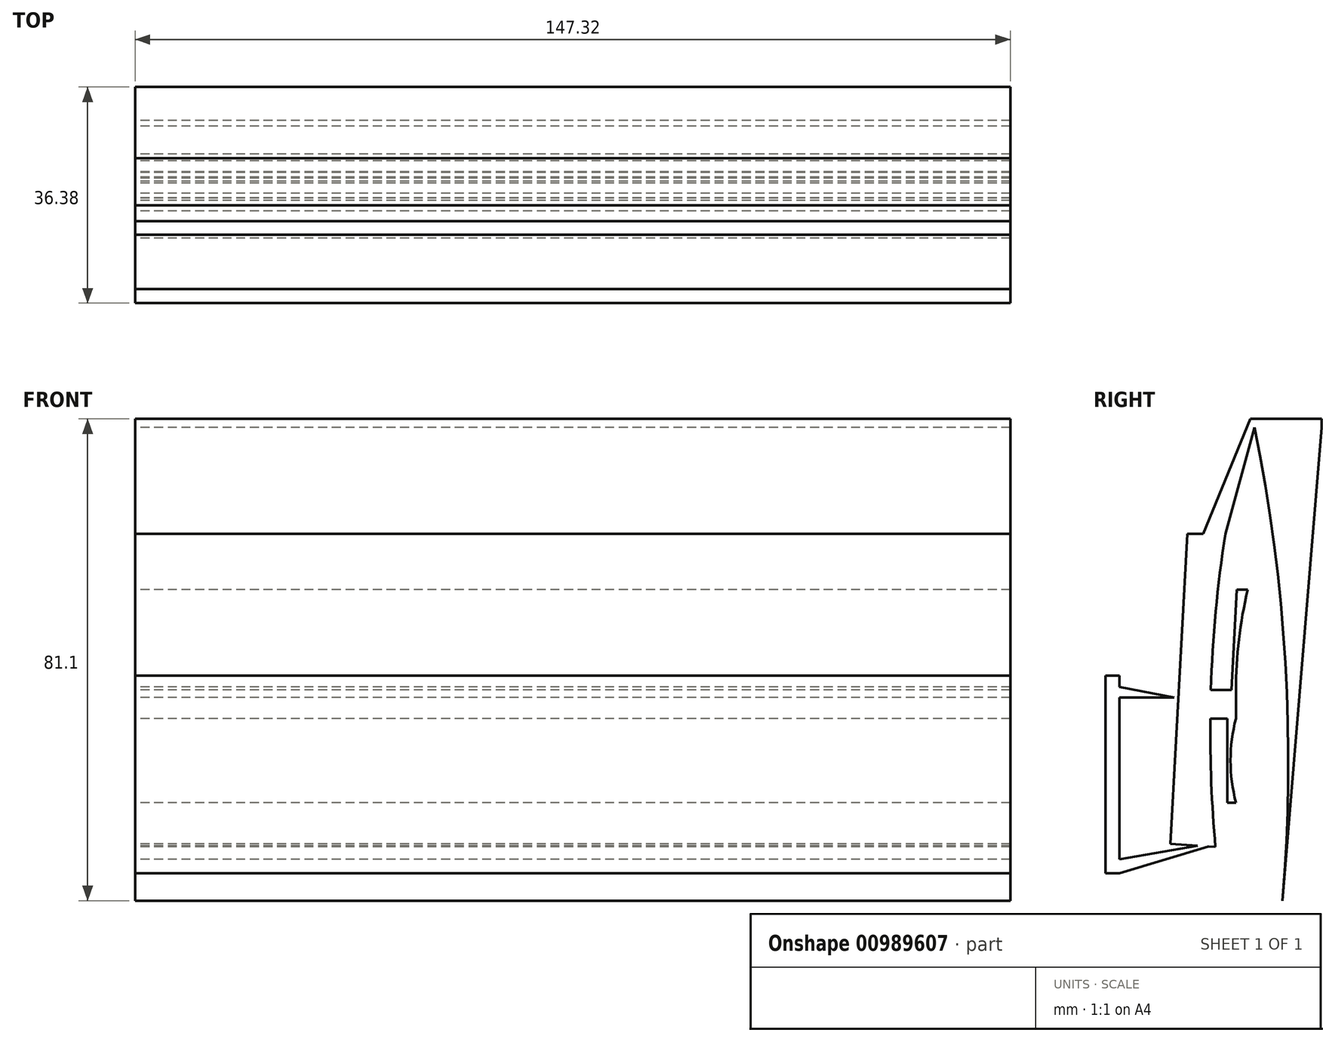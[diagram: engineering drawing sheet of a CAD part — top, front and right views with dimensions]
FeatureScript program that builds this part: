
annotation { "Feature Type Name" : "Feature", "Feature Type Description" : "" }
export const myFeature = defineFeature(function(context is Context, id is Id, definition is map)
    precondition{}
    {
        {
            var Q0;
            Q0=qCreatedBy(makeId("Right.planeOp"),FACE);
            var sketch = newSketch(context, id + "F0", { "sketchPlane" : qUnion([Q0])});
            skArc(sketch, "E0", {"start": v(28.96, -36.84) * mm, "mid": v(29.43, 3.17) * mm, "end": v(24.26, 42.85) * mm});
            skLineSegment(sketch, "E1", {"start": v(28.96, -36.84) * mm, "end": v(35.52, 42.85) * mm});
            skLineSegment(sketch, "E2.top", {"start": v(35.52, 44.26) * mm, "end": v(23.53, 44.26) * mm});
            skLineSegment(sketch, "E2.left", {"start": v(35.52, 42.85) * mm, "end": v(35.52, 44.26) * mm});
            skPoint(sketch, "E3.orphan", {"position": v(17.38, 21.7) * mm});
            skPoint(sketch, "E4.start.orphan", {"position": v(20.82, 21.7) * mm});
            skPoint(sketch, "E5.end.orphan", {"position": v(24.26, 21.7) * mm});
            skLineSegment(sketch, "E6", {"start": v(19.32, 24.94) * mm, "end": v(24.26, 42.85) * mm});
            skArc(sketch, "E7", {"start": v(19.32, 24.94) * mm, "mid": v(17.72, 11.81) * mm, "end": v(16.9, -1.38) * mm});
            skLineSegment(sketch, "E8", {"start": v(16.9, -1.38) * mm, "end": v(20.36, -1.38) * mm});
            skLineSegment(sketch, "E9", {"start": v(21.12, -1.38) * mm, "end": v(21.12, -6.17) * mm});
            skLineSegment(sketch, "E10", {"start": v(19.67, -6.17) * mm, "end": v(16.8, -6.17) * mm});
            skArc(sketch, "E11", {"start": v(23.1, 15.52) * mm, "mid": v(21.62, 7.13) * mm, "end": v(21.12, -1.38) * mm});
            skArc(sketch, "E12", {"start": v(21.12, -6.17) * mm, "mid": v(20.2, -13.25) * mm, "end": v(21.12, -20.33) * mm});
            skLineSegment(sketch, "E13", {"start": v(23.1, 15.52) * mm, "end": v(21.27, 15.52) * mm});
            skLineSegment(sketch, "E14", {"start": v(21.27, 15.52) * mm, "end": v(20.36, -1.38) * mm});
            skLineSegment(sketch, "E15", {"start": v(21.12, -20.33) * mm, "end": v(19.67, -20.33) * mm});
            skLineSegment(sketch, "E16", {"start": v(19.67, -20.33) * mm, "end": v(19.67, -6.17) * mm});
            skLineSegment(sketch, "E17", {"start": v(15.61, 24.94) * mm, "end": v(12.96, 24.94) * mm});
            skLineSegment(sketch, "E18", {"start": v(15.61, 24.94) * mm, "end": v(23.53, 44.26) * mm});
            skLineSegment(sketch, "E19", {"start": v(12.96, 24.94) * mm, "end": v(10.1, -27.29) * mm});
            skLineSegment(sketch, "E20", {"start": v(10.1, -27.29) * mm, "end": v(14.65, -27.6) * mm});
            skLineSegment(sketch, "E21", {"start": v(16.46, -27.72) * mm, "end": v(1.53, -32.25) * mm});
            skLineSegment(sketch, "E22", {"start": v(1.53, -29.9) * mm, "end": v(14.65, -27.6) * mm});
            skLineSegment(sketch, "E23.bottom", {"start": v(1.53, -32.25) * mm, "end": v(-0.86, -32.25) * mm});
            skLineSegment(sketch, "E23.top", {"start": v(1.53, 1.05) * mm, "end": v(-0.86, 1.05) * mm});
            skLineSegment(sketch, "E23.left", {"start": v(1.53, -32.25) * mm, "end": v(1.53, -2.66) * mm});
            skLineSegment(sketch, "E24", {"start": v(1.53, -2.66) * mm, "end": v(10.68, -2.66) * mm});
            skLineSegment(sketch, "E25", {"start": v(10.68, -2.66) * mm, "end": v(1.53, -0.85) * mm});
            skLineSegment(sketch, "E26", {"start": v(-0.86, 1.05) * mm, "end": v(-0.86, -32.25) * mm});
            skPoint(sketch, "E27.orphan", {"position": v(-3.26, 1.05) * mm});
            skLineSegment(sketch, "E28.trimOffspring", {"start": v(1.53, -0.85) * mm, "end": v(1.53, 1.05) * mm});
            skLineSegment(sketch, "E29.trimOffspring", {"start": v(16.46, -27.72) * mm, "end": v(17.66, -27.8) * mm});
            skArc(sketch, "E30.trimOffspring", {"start": v(16.8, -6.17) * mm, "mid": v(16.97, -17) * mm, "end": v(17.66, -27.8) * mm});
            skSolve(sketch);
        }
        {
            var Q0;
            Q0=makeQuery(id+"F0.imprint","IMPRINT",FACE,{"disambiguationData":[TD([[makeQuery(id+"F0.imprint","IMPRINT",EDGE,{"derivedFrom":sQuery(id+"F0.wireOp",EDGE,"E0")}),-1.0]])]});
            var Q1;
            {var subQ3=sQuery(id+"F0.wireOp",EDGE,"E23.bottom");Q1=makeQuery(id+"F0.imprint","IMPRINT",FACE,{"disambiguationData":[TD([[makeQuery(id+"F0.imprint","IMPRINT",EDGE,{"derivedFrom":subQ3}),-1.0]])]});}
            extrude(context, id + "F1", {"entities" : qUnion([Q0, Q1]), "depth" : 147.32 * mm, "offsetDistance" : 25.4 * mm});
        }
    });
